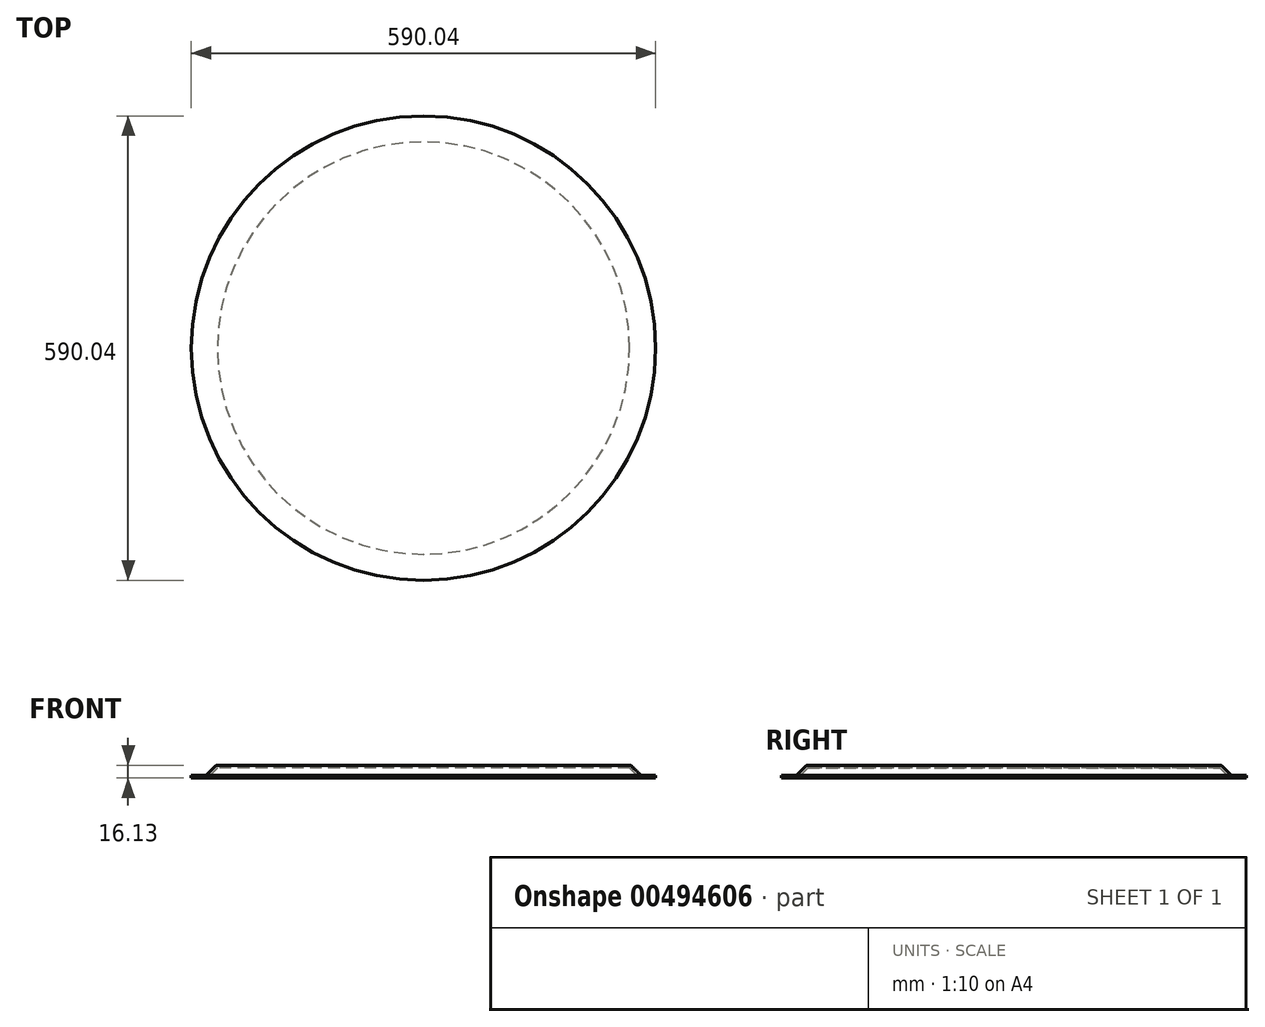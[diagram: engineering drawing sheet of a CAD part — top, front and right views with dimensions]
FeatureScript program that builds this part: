
annotation { "Feature Type Name" : "Feature", "Feature Type Description" : "" }
export const myFeature = defineFeature(function(context is Context, id is Id, definition is map)
    precondition{}
    {
        {
            var Q0;
            Q0=qCreatedBy(makeId("Front.planeOp"),FACE);
            var sketch = newSketch(context, id + "F0", { "sketchPlane" : qUnion([Q0])});
            skLineSegment(sketch, "E0", {"start": v(0, 0) * mm, "end": v(-261.96, 0) * mm});
            skLineSegment(sketch, "E1", {"start": v(-264.2, -0.93) * mm, "end": v(-275.04, -11.77) * mm});
            skLineSegment(sketch, "E2", {"start": v(-277.29, -12.7) * mm, "end": v(-295.02, -12.7) * mm});
            skPoint(sketch, "E3.visualSharp", {"position": v(-263.27, 0) * mm});
            skArc(sketch, "E3.filletArc", {"start": v(-261.96, 0) * mm, "mid": v(-263.17, -0.24) * mm, "end": v(-264.2, -0.93) * mm});
            skPoint(sketch, "E4.visualSharp", {"position": v(-275.97, -12.7) * mm});
            skArc(sketch, "E4.filletArc", {"start": v(-277.29, -12.7) * mm, "mid": v(-276.07, -12.46) * mm, "end": v(-275.04, -11.77) * mm});
            skLineSegment(sketch, "E5.0", {"start": v(-277.29, -16.13) * mm, "end": v(-295.02, -16.13) * mm});
            skArc(sketch, "E5.1", {"start": v(-277.29, -16.13) * mm, "mid": v(-274.76, -15.63) * mm, "end": v(-272.62, -14.2) * mm});
            skLineSegment(sketch, "E5.2", {"start": v(-261.85, -3.43) * mm, "end": v(-272.62, -14.2) * mm});
            skLineSegment(sketch, "E5.3", {"start": v(0, -3.43) * mm, "end": v(-261.85, -3.43) * mm});
            skLineSegment(sketch, "E6", {"start": v(-295.02, -12.7) * mm, "end": v(-295.02, -16.13) * mm});
            skLineSegment(sketch, "E7", {"start": v(0, 0) * mm, "end": v(0, -3.43) * mm});
            skSolve(sketch);
        }
        {
            var Q0;
            Q0=qSketchRegion(id+"F0",true);
            var Q1;
            Q1=sQuery(id+"F0.wireOp",EDGE,"E7");
            revolve(context, id + "F1", {"entities" : qUnion([Q0]), "axis" : qUnion([Q1]), "revolveType" : RevolveType.FULL});
        }
    });
